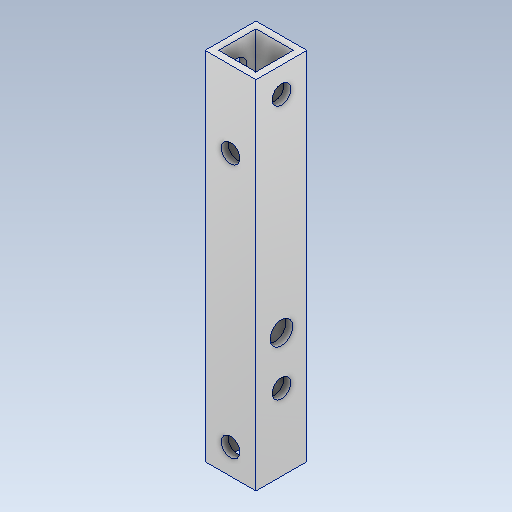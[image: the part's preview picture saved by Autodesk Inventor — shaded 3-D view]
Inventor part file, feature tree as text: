
AUTODESK INVENTOR PART (.ipt)
format: ipt  version: 2020.3 (Build 243373000, 373)  size: 140,800 bytes
history: native  units: mm
features: sketch x4, hole x3, other x1, extrude x1
ambient origin geometry x8: Origin, YZ Plane, XZ Plane, XY Plane, X Axis, Y Axis, Z Axis, Center Point
bodies: Body1 (feature_tree)
feature tree (9):
  other  "ソリッド1"
  extrude  "押し出し1"  Depth=9.0mm
  hole  "穴1"  [1 undecoded]
  hole  "穴2"  [1 undecoded]
  hole  "穴3"  [1 undecoded]
  sketch  "スケッチ1"
  sketch  "スケッチ2"
  sketch  "スケッチ3"
  sketch  "スケッチ4"
note: 3 required parameter values undecoded (feature->parameter linkage not recoverable at this tier; creation-order binding heuristic only, values carry confidence <= 0.55)
